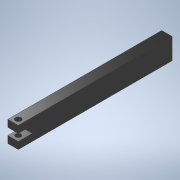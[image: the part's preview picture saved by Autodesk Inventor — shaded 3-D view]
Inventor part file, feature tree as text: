
AUTODESK INVENTOR PART (.ipt)
format: ipt  version: 2020.1 (Build 241239000, 239)  size: 124,416 bytes
history: native  units: in
note: dims shown in document units (in); Inventor stores cm internally (conversion verified against a paired STEP export)
features: extrude x4, sketch x4
ambient origin geometry x8: Origin, YZ Plane, XZ Plane, XY Plane, X Axis, Y Axis, Z Axis, Center Point
bodies: Solid1 (feature_tree)
feature tree (8):
  extrude  "Extrusion1"  Depth=5.5in
  extrude  "Extrusion2"  Depth=0.25in
  extrude  "Extrusion3"  Depth=0.5in TaperAngle=0.0deg
  extrude  "Extrusion4"  Depth=0.1875in
  sketch  "Sketch1"  dims[d0=0.75in d1=5.5in]
  sketch  "Sketch2"  dims[d2=0.375in d3=0.0in d4=0.25in]
  sketch  "Sketch3"  dims[d5=0.5in d6=1.0in d7=0.0in]
  sketch  "Sketch4"  dims[d8=0.205in d9=0.1875in d10=0.25in d11=0.0in d12=0.1875in d13=1.0in d14=0.0in]
